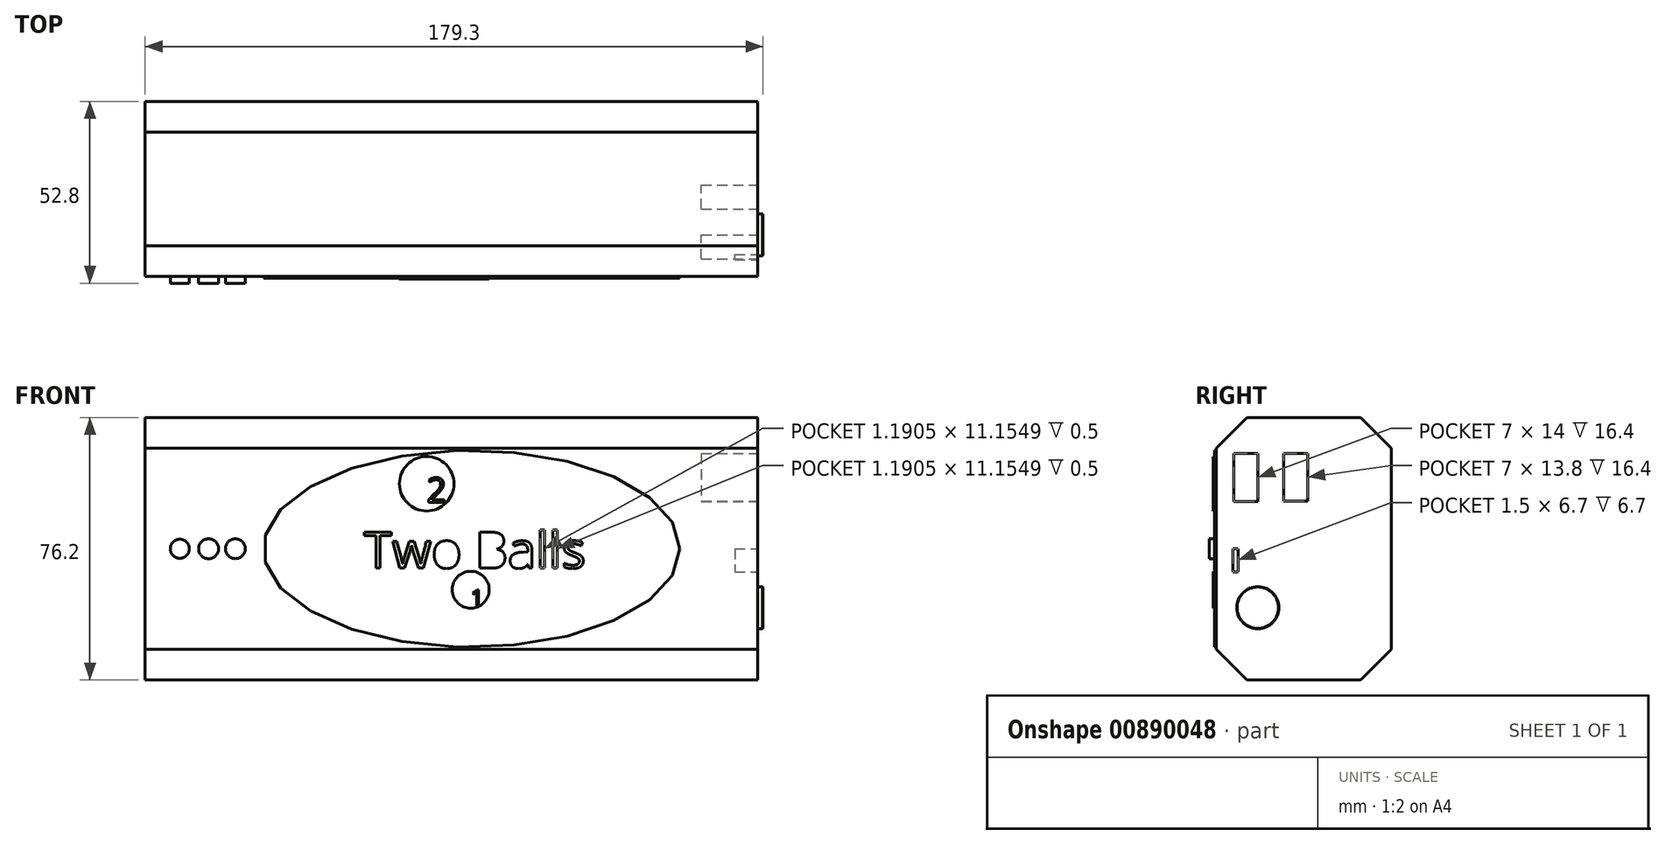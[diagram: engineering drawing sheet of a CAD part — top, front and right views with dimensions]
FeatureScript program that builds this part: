
annotation { "Feature Type Name" : "Feature", "Feature Type Description" : "" }
export const myFeature = defineFeature(function(context is Context, id is Id, definition is map)
    precondition{}
    {
        {
            var Q0;
            Q0=qCreatedBy(makeId("Front.planeOp"),FACE);
            var sketch = newSketch(context, id + "F0", { "sketchPlane" : qUnion([Q0])});
            skLineSegment(sketch, "E0.bottom", {"start": v(63.5, -38.1) * mm, "end": v(-63.5, -38.1) * mm});
            skLineSegment(sketch, "E0.top", {"start": v(63.5, 38.1) * mm, "end": v(-63.5, 38.1) * mm});
            skLineSegment(sketch, "E0.left", {"start": v(63.5, -38.1) * mm, "end": v(63.5, 38.1) * mm});
            skLineSegment(sketch, "E0.right", {"start": v(-63.5, -38.1) * mm, "end": v(-63.5, 38.1) * mm});
            skPoint(sketch, "E0.middle", {"position": v(0, 0) * mm});
            skSolve(sketch);
        }
        {
            var Q0;
            Q0=makeQuery(id+"F0.imprint","IMPRINT",FACE,{"disambiguationData":[TD([[makeQuery(id+"F0.imprint","IMPRINT",EDGE,{"derivedFrom":sQuery(id+"F0.wireOp",EDGE,"E0.bottom")}),-1.0]])]});
            extrude(context, id + "F1", {"entities" : qUnion([Q0]), "depth" : 50.8 * mm, "offsetDistance" : 25.4 * mm});
        }
        {
            var Q0;
            Q0=makeQuery(id+"F1.opExtrude","SWEPT_FACE",FACE,{"disambiguationData":[OSD([sQuery(id+"F0.wireOp",EDGE,"E0.left")])]});
            extrude(context, id + "F2", {"entities" : qUnion([Q0]), "operationType" : NewBodyOperationType.ADD, "depth" : 25.4 * mm, "offsetDistance" : 25.4 * mm});
        }
        {
            var Q0;
            Q0=makeQuery(id+"F2.opExtrude","CAP_FACE",FACE,{"disambiguationData":[OSD([sQuery(id+"F0.wireOp",EDGE,"E0.left")])],"isStart":false});
            extrude(context, id + "F3", {"entities" : qUnion([Q0]), "operationType" : NewBodyOperationType.ADD, "depth" : 25.4 * mm, "offsetDistance" : 25.4 * mm});
        }
        {
            var Q0;
            Q0=makeQuery(id+"F3.opExtrude","CAP_FACE",FACE,{"disambiguationData":[OSD([sQuery(id+"F0.wireOp",EDGE,"E0.left")])],"isStart":false});
            var sketch = newSketch(context, id + "F4", { "sketchPlane" : qUnion([Q0])});
            skLineSegment(sketch, "E1.bottom", {"start": v(-45.72, 27.67) * mm, "end": v(-38.72, 27.67) * mm});
            skLineSegment(sketch, "E1.top", {"start": v(-45.72, 13.67) * mm, "end": v(-38.72, 13.67) * mm});
            skLineSegment(sketch, "E1.left", {"start": v(-45.72, 27.67) * mm, "end": v(-45.72, 13.67) * mm});
            skLineSegment(sketch, "E1.right", {"start": v(-38.72, 27.67) * mm, "end": v(-38.72, 13.67) * mm});
            skSolve(sketch);
        }
        {
            var Q0;
            Q0=makeQuery(id+"F4.imprint","IMPRINT",FACE,{"disambiguationData":[TD([[makeQuery(id+"F4.imprint","IMPRINT",EDGE,{"derivedFrom":sQuery(id+"F4.wireOp",EDGE,"E1.bottom")}),-1.0]])]});
            var sketch = newSketch(context, id + "F5", { "sketchPlane" : qUnion([Q0])});
            skSolve(sketch);
        }
        {
            var Q0;
            Q0 = qSketchRegion(id + "F5", true);
            var Q1;
            Q1=makeQuery(id+"F4.imprint","IMPRINT",FACE,{"disambiguationData":[TD([[makeQuery(id+"F4.imprint","IMPRINT",EDGE,{"derivedFrom":sQuery(id+"F4.wireOp",EDGE,"E1.bottom")}),-1.0]])]});
            extrude(context, id + "F6", {"entities" : qUnion([Q0, Q1]), "operationType" : NewBodyOperationType.REMOVE, "oppositeDirection" : true, "depth" : 16.4 * mm, "offsetDistance" : 25.4 * mm});
        }
        {
            var Q0;
            Q0=makeQuery(id+"F3.opExtrude","CAP_FACE",FACE,{"disambiguationData":[OSD([sQuery(id+"F0.wireOp",EDGE,"E0.left")])],"isStart":false});
            var sketch = newSketch(context, id + "F7", { "sketchPlane" : qUnion([Q0])});
            skLineSegment(sketch, "E2.bottom", {"start": v(-31.23, 27.67) * mm, "end": v(-24.23, 27.67) * mm});
            skLineSegment(sketch, "E2.top", {"start": v(-31.23, 13.87) * mm, "end": v(-24.23, 13.87) * mm});
            skLineSegment(sketch, "E2.left", {"start": v(-31.23, 27.67) * mm, "end": v(-31.23, 13.87) * mm});
            skLineSegment(sketch, "E2.right", {"start": v(-24.23, 27.67) * mm, "end": v(-24.23, 13.87) * mm});
            skSolve(sketch);
        }
        {
            var Q0;
            Q0=makeQuery(id+"F7.imprint","IMPRINT",FACE,{"disambiguationData":[TD([[makeQuery(id+"F7.imprint","IMPRINT",EDGE,{"derivedFrom":sQuery(id+"F7.wireOp",EDGE,"E2.bottom")}),-1.0]])]});
            extrude(context, id + "F8", {"entities" : qUnion([Q0]), "operationType" : NewBodyOperationType.REMOVE, "oppositeDirection" : true, "depth" : 16.4 * mm, "offsetDistance" : 25.4 * mm});
        }
        {
            var Q0;
            Q0=makeQuery(id+"F3.opExtrude","CAP_FACE",FACE,{"disambiguationData":[OSD([sQuery(id+"F0.wireOp",EDGE,"E0.left")])],"isStart":false});
            var sketch = newSketch(context, id + "F9", { "sketchPlane" : qUnion([Q0])});
            skCircle(sketch, "E3", {"center": v(-38.72, -17.12) * mm, "radius": 6.13 * mm});
            skCircle(sketch, "E4", {"center": v(-38.72, -17.12) * mm, "radius": 6.01 * mm});
            skSolve(sketch);
        }
        {
            var Q0;
            Q0 = qSketchRegion(id + "F9", true);
            extrude(context, id + "F10", {"entities" : qUnion([Q0]), "operationType" : NewBodyOperationType.ADD, "depth" : 1.3 * mm, "offsetDistance" : 25.4 * mm});
        }
        {
            var Q0;
            Q0=makeQuery(id+"F10.boolean.opBoolean","SPLIT",FACE,{"disambiguationData":[TD([makeQuery(id+"F10.opExtrude","SWEPT_FACE",FACE,{"disambiguationData":[OSD([sQuery(id+"F9.wireOp",EDGE,"E4")])]})])],"derivedFrom":makeQuery(id+"F3.opExtrude","CAP_FACE",FACE,{"disambiguationData":[OSD([sQuery(id+"F0.wireOp",EDGE,"E0.left")])],"isStart":false})});
            extrude(context, id + "F11", {"entities" : qUnion([Q0]), "operationType" : NewBodyOperationType.ADD, "depth" : 1.5 * mm, "offsetDistance" : 25.4 * mm});
        }
        {
            var Q0;
            {var subQ0=sQuery(id+"F0.wireOp",EDGE,"E0.left");var subQ6=sQuery(id+"F0.wireOp",EDGE,"E0.bottom");Q0=makeQuery(id+"F10.boolean.opBoolean","SPLIT",FACE,{"disambiguationData":[TD([makeQuery(id+"F1.opExtrude","SWEPT_FACE",FACE,{"disambiguationData":[OSD([subQ6])]})])],"derivedFrom":makeQuery(id+"F3.opExtrude","CAP_FACE",FACE,{"disambiguationData":[OSD([subQ0])],"isStart":false})});}
            var sketch = newSketch(context, id + "F12", { "sketchPlane" : qUnion([Q0])});
            skPoint(sketch, "E5.firstSnap0", {"position": v(-50.8, 0) * mm});
            skLineSegment(sketch, "E5.bottom", {"start": v(-45.9, 0) * mm, "end": v(-44.4, 0) * mm});
            skLineSegment(sketch, "E5.top", {"start": v(-45.9, -6.7) * mm, "end": v(-44.4, -6.7) * mm});
            skLineSegment(sketch, "E5.left", {"start": v(-45.9, 0) * mm, "end": v(-45.9, -6.7) * mm});
            skLineSegment(sketch, "E5.right", {"start": v(-44.4, 0) * mm, "end": v(-44.4, -6.7) * mm});
            skSolve(sketch);
        }
        {
            var Q0;
            Q0=makeQuery(id+"F12.imprint","IMPRINT",FACE,{"disambiguationData":[TD([[makeQuery(id+"F12.imprint","IMPRINT",EDGE,{"derivedFrom":sQuery(id+"F12.wireOp",EDGE,"E5.bottom")}),-1.0]])]});
            extrude(context, id + "F13", {"entities" : qUnion([Q0]), "operationType" : NewBodyOperationType.REMOVE, "oppositeDirection" : true, "depth" : 6.7 * mm, "offsetDistance" : 25.4 * mm});
        }
        {
            var Q0;
            {var subQ0=sQuery(id+"F0.wireOp",EDGE,"E0.left");var subQ1=makeQuery(id+"F1.opExtrude","CAP_EDGE",EDGE,{"disambiguationData":[OSD([subQ0])],"isStart":false});Q0=makeQuery(id+"F3.boolean.opBoolean","MERGE",FACE,{"derivedFrom":[makeQuery(id+"F2.boolean.opBoolean","MERGE",FACE,{"derivedFrom":[makeQuery(id+"F1.opExtrude","CAP_FACE",FACE,{"disambiguationData":[OSD([sQuery(id+"F0.wireOp",EDGE,"E0.bottom"),sQuery(id+"F0.wireOp",EDGE,"E0.top"),subQ0,sQuery(id+"F0.wireOp",EDGE,"E0.right")])],"isStart":false}),makeQuery(id+"F2.opExtrude","SWEPT_FACE",FACE,{"disambiguationData":[OSD([subQ0]),TDD([subQ1])]})]}),makeQuery(id+"F3.opExtrude","SWEPT_FACE",FACE,{"disambiguationData":[OSD([subQ0]),TDD([makeQuery(id+"F2.opExtrude","CAP_EDGE",EDGE,{"disambiguationData":[OSD([subQ0]),TDD([subQ1])],"isStart":false})])]})]});}
            var sketch = newSketch(context, id + "F14", { "sketchPlane" : qUnion([Q0])});
            skCircle(sketch, "E6", {"center": v(-53.45, 0) * mm, "radius": 2.76 * mm});
            skPoint(sketch, "E6.centerSnap0", {"position": v(-63.5, 0) * mm});
            skCircle(sketch, "E7", {"center": v(-45.1, 0) * mm, "radius": 2.9 * mm});
            skCircle(sketch, "E8", {"center": v(-37.33, 0) * mm, "radius": 2.88 * mm});
            skSolve(sketch);
        }
        {
            var Q0;
            Q0=makeQuery(id+"F14.imprint","IMPRINT",FACE,{"disambiguationData":[TD([[makeQuery(id+"F14.imprint","IMPRINT",EDGE,{"derivedFrom":sQuery(id+"F14.wireOp",EDGE,"E6")}),1.0]])]});
            var Q1;
            Q1=makeQuery(id+"F14.imprint","IMPRINT",FACE,{"disambiguationData":[TD([[makeQuery(id+"F14.imprint","IMPRINT",EDGE,{"derivedFrom":sQuery(id+"F14.wireOp",EDGE,"E7")}),1.0]])]});
            var Q2;
            Q2=makeQuery(id+"F14.imprint","IMPRINT",FACE,{"disambiguationData":[TD([[makeQuery(id+"F14.imprint","IMPRINT",EDGE,{"derivedFrom":sQuery(id+"F14.wireOp",EDGE,"E8")}),1.0]])]});
            extrude(context, id + "F15", {"entities" : qUnion([Q0, Q1, Q2]), "operationType" : NewBodyOperationType.ADD, "depth" : 2 * mm, "offsetDistance" : 25.4 * mm});
        }
        {
            var Q0;
            {var subQ0=sQuery(id+"F0.wireOp",EDGE,"E0.left");var subQ1=makeQuery(id+"F1.opExtrude","CAP_EDGE",EDGE,{"disambiguationData":[OSD([subQ0])],"isStart":false});Q0=makeQuery(id+"F3.boolean.opBoolean","MERGE",FACE,{"derivedFrom":[makeQuery(id+"F2.boolean.opBoolean","MERGE",FACE,{"derivedFrom":[makeQuery(id+"F1.opExtrude","CAP_FACE",FACE,{"disambiguationData":[OSD([sQuery(id+"F0.wireOp",EDGE,"E0.bottom"),sQuery(id+"F0.wireOp",EDGE,"E0.top"),subQ0,sQuery(id+"F0.wireOp",EDGE,"E0.right")])],"isStart":false}),makeQuery(id+"F2.opExtrude","SWEPT_FACE",FACE,{"disambiguationData":[OSD([subQ0]),TDD([subQ1])]})]}),makeQuery(id+"F3.opExtrude","SWEPT_FACE",FACE,{"disambiguationData":[OSD([subQ0]),TDD([makeQuery(id+"F2.opExtrude","CAP_EDGE",EDGE,{"disambiguationData":[OSD([subQ0]),TDD([subQ1])],"isStart":false})])]})]});}
            var sketch = newSketch(context, id + "F16", { "sketchPlane" : qUnion([Q0])});
            skEllipse(sketch, "E9", {"center": v(31.27, 0) * mm, "majorRadius": 60.4 * mm, "minorRadius": 28.6 * mm, "majorAxis": v(1, 0)});
            skText(sketch, "E10", { "text": "Two Balls", "fontName": "OpenSans-Regular.ttf"});
            const initialGuessF16  = {"E10": [0, -0.00564, 1, 0, 0.01057]};
            skSetInitialGuess(sketch, initialGuessF16);
            skSolve(sketch);
        }
        {
            var Q0;
            Q0 = qSketchRegion(id + "F16", true);
            extrude(context, id + "F17", {"entities" : qUnion([Q0]), "operationType" : NewBodyOperationType.ADD, "depth" : .5 * mm, "offsetDistance" : 25.4 * mm});
        }
        {
            var Q0;
            {var subQ0=sQuery(id+"F0.wireOp",EDGE,"E0.left");var subQ1=sQuery(id+"F0.wireOp",EDGE,"E0.top");var subQ2=makeQuery(id+"F1.opExtrude","CAP_VERTEX",VERTEX,{"disambiguationData":[OSD([subQ1,subQ0])],"isStart":false});Q0=makeQuery(id+"F3.boolean.opBoolean","MERGE",EDGE,{"derivedFrom":[makeQuery(id+"F2.boolean.opBoolean","MERGE",EDGE,{"derivedFrom":[makeQuery(id+"F1.opExtrude","CAP_EDGE",EDGE,{"disambiguationData":[OSD([subQ1])],"isStart":false}),makeQuery(id+"F2.opExtrude","SWEPT_EDGE",EDGE,{"disambiguationData":[OSD([subQ1,subQ0]),TDD([subQ2])]})]}),makeQuery(id+"F3.opExtrude","SWEPT_EDGE",EDGE,{"disambiguationData":[OSD([subQ1,subQ0]),TDD([makeQuery(id+"F2.opExtrude","CAP_VERTEX",VERTEX,{"disambiguationData":[OSD([subQ1,subQ0]),TDD([subQ2])],"isStart":false})])]})]});}
            var Q1;
            {var subQ0=sQuery(id+"F0.wireOp",EDGE,"E0.left");var subQ1=sQuery(id+"F0.wireOp",EDGE,"E0.top");var subQ2=makeQuery(id+"F1.opExtrude","CAP_VERTEX",VERTEX,{"disambiguationData":[OSD([subQ1,subQ0])],"isStart":true});Q1=makeQuery(id+"F3.boolean.opBoolean","MERGE",EDGE,{"derivedFrom":[makeQuery(id+"F2.boolean.opBoolean","MERGE",EDGE,{"derivedFrom":[makeQuery(id+"F1.opExtrude","CAP_EDGE",EDGE,{"disambiguationData":[OSD([subQ1])],"isStart":true}),makeQuery(id+"F2.opExtrude","SWEPT_EDGE",EDGE,{"disambiguationData":[OSD([subQ1,subQ0]),TDD([subQ2])]})]}),makeQuery(id+"F3.opExtrude","SWEPT_EDGE",EDGE,{"disambiguationData":[OSD([subQ1,subQ0]),TDD([makeQuery(id+"F2.opExtrude","CAP_VERTEX",VERTEX,{"disambiguationData":[OSD([subQ1,subQ0]),TDD([subQ2])],"isStart":false})])]})]});}
            var Q2;
            {var subQ0=sQuery(id+"F0.wireOp",EDGE,"E0.left");var subQ1=sQuery(id+"F0.wireOp",EDGE,"E0.bottom");var subQ2=makeQuery(id+"F1.opExtrude","CAP_VERTEX",VERTEX,{"disambiguationData":[OSD([subQ1,subQ0])],"isStart":false});Q2=makeQuery(id+"F3.boolean.opBoolean","MERGE",EDGE,{"derivedFrom":[makeQuery(id+"F2.boolean.opBoolean","MERGE",EDGE,{"derivedFrom":[makeQuery(id+"F1.opExtrude","CAP_EDGE",EDGE,{"disambiguationData":[OSD([subQ1])],"isStart":false}),makeQuery(id+"F2.opExtrude","SWEPT_EDGE",EDGE,{"disambiguationData":[OSD([subQ1,subQ0]),TDD([subQ2])]})]}),makeQuery(id+"F3.opExtrude","SWEPT_EDGE",EDGE,{"disambiguationData":[OSD([subQ1,subQ0]),TDD([makeQuery(id+"F2.opExtrude","CAP_VERTEX",VERTEX,{"disambiguationData":[OSD([subQ1,subQ0]),TDD([subQ2])],"isStart":false})])]})]});}
            var Q3;
            {var subQ0=sQuery(id+"F0.wireOp",EDGE,"E0.left");var subQ1=sQuery(id+"F0.wireOp",EDGE,"E0.bottom");var subQ2=makeQuery(id+"F1.opExtrude","CAP_VERTEX",VERTEX,{"disambiguationData":[OSD([subQ1,subQ0])],"isStart":true});Q3=makeQuery(id+"F3.boolean.opBoolean","MERGE",EDGE,{"derivedFrom":[makeQuery(id+"F2.boolean.opBoolean","MERGE",EDGE,{"derivedFrom":[makeQuery(id+"F1.opExtrude","CAP_EDGE",EDGE,{"disambiguationData":[OSD([subQ1])],"isStart":true}),makeQuery(id+"F2.opExtrude","SWEPT_EDGE",EDGE,{"disambiguationData":[OSD([subQ1,subQ0]),TDD([subQ2])]})]}),makeQuery(id+"F3.opExtrude","SWEPT_EDGE",EDGE,{"disambiguationData":[OSD([subQ1,subQ0]),TDD([makeQuery(id+"F2.opExtrude","CAP_VERTEX",VERTEX,{"disambiguationData":[OSD([subQ1,subQ0]),TDD([subQ2])],"isStart":false})])]})]});}
            chamfer(context, id + "F18", {"entities" : qUnion([Q0, Q1, Q2, Q3]), "width" : 8.9 * mm, "tangentPropagation" : true});
        }
        {
            var Q0;
            Q0=makeQuery(id+"F17.opExtrude","CAP_FACE",FACE,{"disambiguationData":[OSD([sQuery(id+"F16.wireOp",EDGE,"E9"),sQuery(id+"F16.wireOp",EDGE,"E10.sketch_text.stroke-0"),sQuery(id+"F16.wireOp",EDGE,"E10.sketch_text.stroke-1"),sQuery(id+"F16.wireOp",EDGE,"E10.sketch_text.stroke-2"),sQuery(id+"F16.wireOp",EDGE,"E10.sketch_text.stroke-3"),sQuery(id+"F16.wireOp",EDGE,"E10.sketch_text.stroke-4"),sQuery(id+"F16.wireOp",EDGE,"E10.sketch_text.stroke-5"),sQuery(id+"F16.wireOp",EDGE,"E10.sketch_text.stroke-6"),sQuery(id+"F16.wireOp",EDGE,"E10.sketch_text.stroke-7"),sQuery(id+"F16.wireOp",EDGE,"E10.sketch_text.stroke-8"),sQuery(id+"F16.wireOp",EDGE,"E10.sketch_text.stroke-9"),sQuery(id+"F16.wireOp",EDGE,"E10.sketch_text.stroke-10"),sQuery(id+"F16.wireOp",EDGE,"E10.sketch_text.stroke-11"),sQuery(id+"F16.wireOp",EDGE,"E10.sketch_text.stroke-12"),sQuery(id+"F16.wireOp",EDGE,"E10.sketch_text.stroke-13"),sQuery(id+"F16.wireOp",EDGE,"E10.sketch_text.stroke-14"),sQuery(id+"F16.wireOp",EDGE,"E10.sketch_text.stroke-15"),sQuery(id+"F16.wireOp",EDGE,"E10.sketch_text.stroke-16"),sQuery(id+"F16.wireOp",EDGE,"E10.sketch_text.stroke-17"),sQuery(id+"F16.wireOp",EDGE,"E10.sketch_text.stroke-18"),sQuery(id+"F16.wireOp",EDGE,"E10.sketch_text.stroke-19"),sQuery(id+"F16.wireOp",EDGE,"E10.sketch_text.stroke-20"),sQuery(id+"F16.wireOp",EDGE,"E10.sketch_text.stroke-21"),sQuery(id+"F16.wireOp",EDGE,"E10.sketch_text.stroke-22"),sQuery(id+"F16.wireOp",EDGE,"E10.sketch_text.stroke-23"),sQuery(id+"F16.wireOp",EDGE,"E10.sketch_text.stroke-24"),sQuery(id+"F16.wireOp",EDGE,"E10.sketch_text.stroke-25"),sQuery(id+"F16.wireOp",EDGE,"E10.sketch_text.stroke-26"),sQuery(id+"F16.wireOp",EDGE,"E10.sketch_text.stroke-27"),sQuery(id+"F16.wireOp",EDGE,"E10.sketch_text.stroke-28"),sQuery(id+"F16.wireOp",EDGE,"E10.sketch_text.stroke-29"),sQuery(id+"F16.wireOp",EDGE,"E10.sketch_text.stroke-30"),sQuery(id+"F16.wireOp",EDGE,"E10.sketch_text.stroke-31"),sQuery(id+"F16.wireOp",EDGE,"E10.sketch_text.stroke-32"),sQuery(id+"F16.wireOp",EDGE,"E10.sketch_text.stroke-33"),sQuery(id+"F16.wireOp",EDGE,"E10.sketch_text.stroke-34"),sQuery(id+"F16.wireOp",EDGE,"E10.sketch_text.stroke-35"),sQuery(id+"F16.wireOp",EDGE,"E10.sketch_text.stroke-36"),sQuery(id+"F16.wireOp",EDGE,"E10.sketch_text.stroke-37"),sQuery(id+"F16.wireOp",EDGE,"E10.sketch_text.stroke-38"),sQuery(id+"F16.wireOp",EDGE,"E10.sketch_text.stroke-39"),sQuery(id+"F16.wireOp",EDGE,"E10.sketch_text.stroke-48"),sQuery(id+"F16.wireOp",EDGE,"E10.sketch_text.stroke-49"),sQuery(id+"F16.wireOp",EDGE,"E10.sketch_text.stroke-50"),sQuery(id+"F16.wireOp",EDGE,"E10.sketch_text.stroke-51"),sQuery(id+"F16.wireOp",EDGE,"E10.sketch_text.stroke-52"),sQuery(id+"F16.wireOp",EDGE,"E10.sketch_text.stroke-53"),sQuery(id+"F16.wireOp",EDGE,"E10.sketch_text.stroke-54"),sQuery(id+"F16.wireOp",EDGE,"E10.sketch_text.stroke-55"),sQuery(id+"F16.wireOp",EDGE,"E10.sketch_text.stroke-56"),sQuery(id+"F16.wireOp",EDGE,"E10.sketch_text.stroke-57"),sQuery(id+"F16.wireOp",EDGE,"E10.sketch_text.stroke-58"),sQuery(id+"F16.wireOp",EDGE,"E10.sketch_text.stroke-73"),sQuery(id+"F16.wireOp",EDGE,"E10.sketch_text.stroke-74"),sQuery(id+"F16.wireOp",EDGE,"E10.sketch_text.stroke-75"),sQuery(id+"F16.wireOp",EDGE,"E10.sketch_text.stroke-76"),sQuery(id+"F16.wireOp",EDGE,"E10.sketch_text.stroke-77"),sQuery(id+"F16.wireOp",EDGE,"E10.sketch_text.stroke-78"),sQuery(id+"F16.wireOp",EDGE,"E10.sketch_text.stroke-79"),sQuery(id+"F16.wireOp",EDGE,"E10.sketch_text.stroke-80"),sQuery(id+"F16.wireOp",EDGE,"E10.sketch_text.stroke-81"),sQuery(id+"F16.wireOp",EDGE,"E10.sketch_text.stroke-82"),sQuery(id+"F16.wireOp",EDGE,"E10.sketch_text.stroke-83"),sQuery(id+"F16.wireOp",EDGE,"E10.sketch_text.stroke-84"),sQuery(id+"F16.wireOp",EDGE,"E10.sketch_text.stroke-85"),sQuery(id+"F16.wireOp",EDGE,"E10.sketch_text.stroke-86"),sQuery(id+"F16.wireOp",EDGE,"E10.sketch_text.stroke-87"),sQuery(id+"F16.wireOp",EDGE,"E10.sketch_text.stroke-88"),sQuery(id+"F16.wireOp",EDGE,"E10.sketch_text.stroke-89"),sQuery(id+"F16.wireOp",EDGE,"E10.sketch_text.stroke-90"),sQuery(id+"F16.wireOp",EDGE,"E10.sketch_text.stroke-91"),sQuery(id+"F16.wireOp",EDGE,"E10.sketch_text.stroke-100"),sQuery(id+"F16.wireOp",EDGE,"E10.sketch_text.stroke-101"),sQuery(id+"F16.wireOp",EDGE,"E10.sketch_text.stroke-102"),sQuery(id+"F16.wireOp",EDGE,"E10.sketch_text.stroke-103"),sQuery(id+"F16.wireOp",EDGE,"E10.sketch_text.stroke-104"),sQuery(id+"F16.wireOp",EDGE,"E10.sketch_text.stroke-105"),sQuery(id+"F16.wireOp",EDGE,"E10.sketch_text.stroke-106"),sQuery(id+"F16.wireOp",EDGE,"E10.sketch_text.stroke-107"),sQuery(id+"F16.wireOp",EDGE,"E10.sketch_text.stroke-108"),sQuery(id+"F16.wireOp",EDGE,"E10.sketch_text.stroke-109"),sQuery(id+"F16.wireOp",EDGE,"E10.sketch_text.stroke-110"),sQuery(id+"F16.wireOp",EDGE,"E10.sketch_text.stroke-111"),sQuery(id+"F16.wireOp",EDGE,"E10.sketch_text.stroke-112"),sQuery(id+"F16.wireOp",EDGE,"E10.sketch_text.stroke-113"),sQuery(id+"F16.wireOp",EDGE,"E10.sketch_text.stroke-114"),sQuery(id+"F16.wireOp",EDGE,"E10.sketch_text.stroke-115"),sQuery(id+"F16.wireOp",EDGE,"E10.sketch_text.stroke-116"),sQuery(id+"F16.wireOp",EDGE,"E10.sketch_text.stroke-117"),sQuery(id+"F16.wireOp",EDGE,"E10.sketch_text.stroke-118"),sQuery(id+"F16.wireOp",EDGE,"E10.sketch_text.stroke-119"),sQuery(id+"F16.wireOp",EDGE,"E10.sketch_text.stroke-120"),sQuery(id+"F16.wireOp",EDGE,"E10.sketch_text.stroke-121"),sQuery(id+"F16.wireOp",EDGE,"E10.sketch_text.stroke-122"),sQuery(id+"F16.wireOp",EDGE,"E10.sketch_text.stroke-123"),sQuery(id+"F16.wireOp",EDGE,"E10.sketch_text.stroke-124"),sQuery(id+"F16.wireOp",EDGE,"E10.sketch_text.stroke-125"),sQuery(id+"F16.wireOp",EDGE,"E10.sketch_text.stroke-126"),sQuery(id+"F16.wireOp",EDGE,"E10.sketch_text.stroke-127"),sQuery(id+"F16.wireOp",EDGE,"E10.sketch_text.stroke-128"),sQuery(id+"F16.wireOp",EDGE,"E10.sketch_text.stroke-129"),sQuery(id+"F16.wireOp",EDGE,"E10.sketch_text.stroke-130"),sQuery(id+"F16.wireOp",EDGE,"E10.sketch_text.stroke-131"),sQuery(id+"F16.wireOp",EDGE,"E10.sketch_text.stroke-132")])],"isStart":false});
            var sketch = newSketch(context, id + "F19", { "sketchPlane" : qUnion([Q0])});
            skCircle(sketch, "E11", {"center": v(18.2, 18.88) * mm, "radius": 7.91 * mm});
            skCircle(sketch, "E12", {"center": v(30.98, -11.9) * mm, "radius": 5.35 * mm});
            skText(sketch, "E13", { "text": "2\n", "fontName": "OpenSans-Regular.ttf"});
            skText(sketch, "E14", { "text": "1", "fontName": "OpenSans-Regular.ttf"});
            const initialGuessF19  = {"E13": [0.0182, 0.0135, 1, 0, 0.00717], "E14": [0.03098, -0.01655, 1, 0, 0.00464]};
            skSetInitialGuess(sketch, initialGuessF19);
            skSolve(sketch);
        }
        {
            var Q0;
            Q0 = qSketchRegion(id + "F19", true);
            extrude(context, id + "F20", {"entities" : qUnion([Q0]), "operationType" : NewBodyOperationType.ADD, "depth" : .3 * mm, "offsetDistance" : 25.4 * mm});
        }
    });
